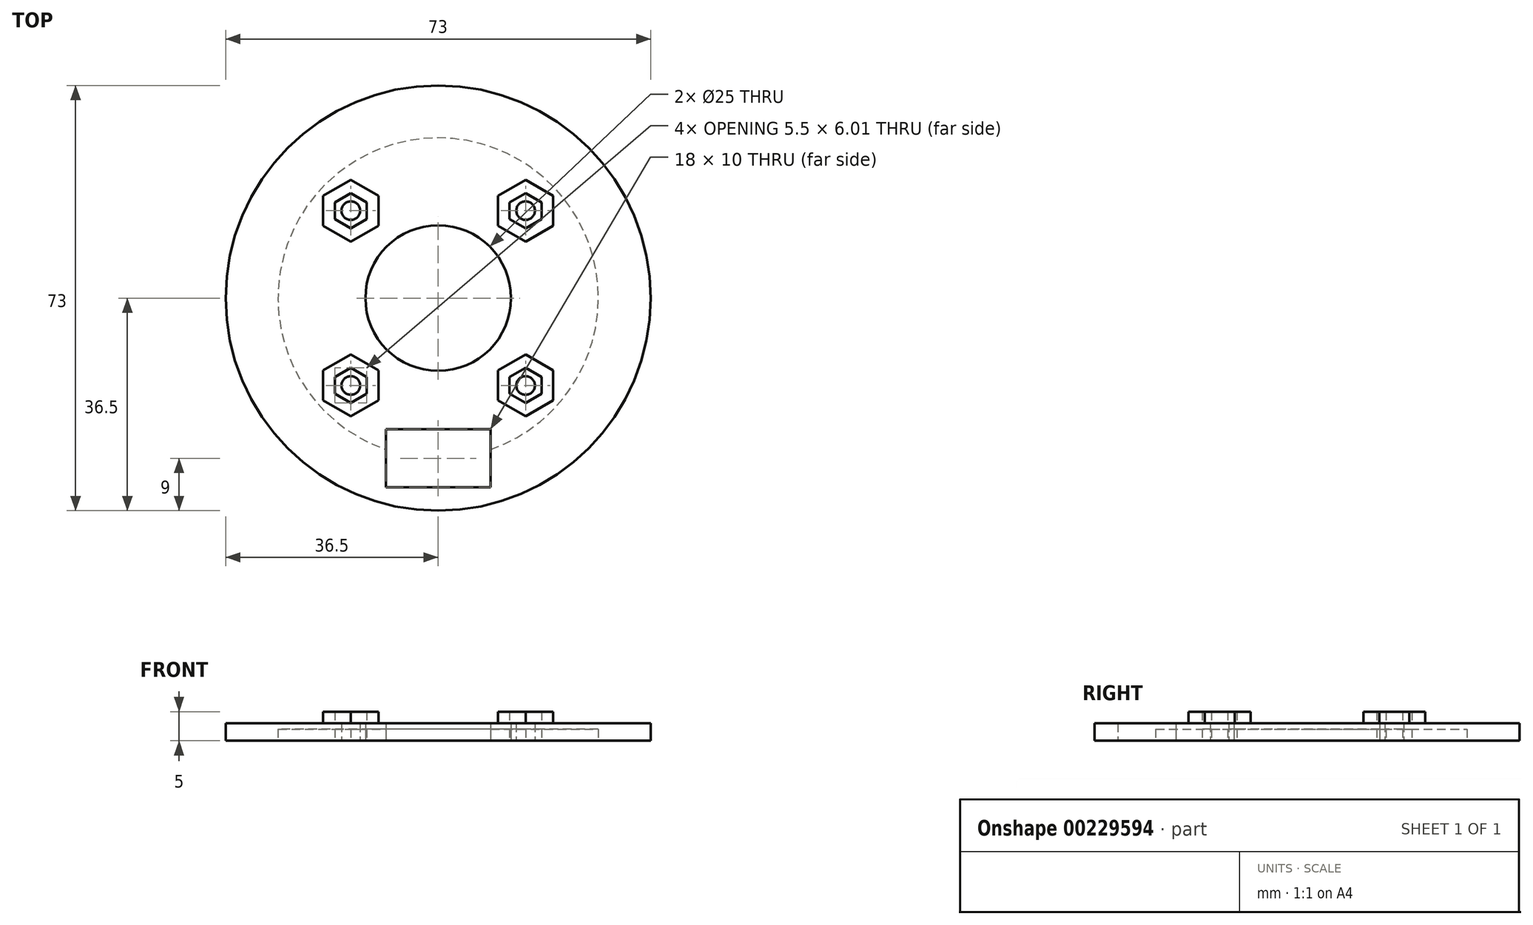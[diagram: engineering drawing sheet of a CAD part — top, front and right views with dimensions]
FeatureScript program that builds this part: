
annotation { "Feature Type Name" : "Feature", "Feature Type Description" : "" }
export const myFeature = defineFeature(function(context is Context, id is Id, definition is map)
    precondition{}
    {
        {
            var Q0;
            Q0=qCreatedBy(makeId("Top.planeOp"),FACE);
            var sketch = newSketch(context, id + "F0", { "sketchPlane" : qUnion([Q0])});
            skCircle(sketch, "E0", {"center": v(-15, 15) * mm, "radius": 1.6 * mm});
            skCircle(sketch, "E1", {"center": v(0, 0) * mm, "radius": 12.5 * mm});
            skLineSegment(sketch, "E2.bottom", {"start": v(9, -32.5) * mm, "end": v(-9, -32.5) * mm});
            skLineSegment(sketch, "E2.top", {"start": v(9, -22.5) * mm, "end": v(-9, -22.5) * mm});
            skLineSegment(sketch, "E2.left", {"start": v(9, -32.5) * mm, "end": v(9, -22.5) * mm});
            skLineSegment(sketch, "E2.right", {"start": v(-9, -32.5) * mm, "end": v(-9, -22.5) * mm});
            skPoint(sketch, "E2.middle", {"position": v(0, -27.5) * mm});
            skCircle(sketch, "E3", {"center": v(0, 0) * mm, "radius": 36.5 * mm});
            skLineSegment(sketch, "E4", {"start": v(-17.75, 16.42) * mm, "end": v(-17.75, 13.58) * mm});
            skLineSegment(sketch, "E5", {"start": v(-12.25, 16.42) * mm, "end": v(-12.25, 13.58) * mm});
            skLineSegment(sketch, "E6", {"start": v(-17.75, 16.42) * mm, "end": v(-15, 18) * mm});
            skLineSegment(sketch, "E7", {"start": v(-15, 18) * mm, "end": v(-12.25, 16.42) * mm});
            skLineSegment(sketch, "E8", {"start": v(-17.75, 13.58) * mm, "end": v(-15, 12) * mm});
            skLineSegment(sketch, "E9", {"start": v(-15, 12) * mm, "end": v(-12.25, 13.58) * mm});
            skLineSegment(sketch, "E10.0", {"start": v(-19.75, 12.43) * mm, "end": v(-15, 9.69) * mm});
            skLineSegment(sketch, "E10.1", {"start": v(-10.25, 17.57) * mm, "end": v(-10.25, 12.43) * mm});
            skLineSegment(sketch, "E10.2", {"start": v(-15, 20.31) * mm, "end": v(-10.25, 17.57) * mm});
            skLineSegment(sketch, "E10.3", {"start": v(-15, 9.69) * mm, "end": v(-10.25, 12.43) * mm});
            skLineSegment(sketch, "E10.4", {"start": v(-19.75, 17.57) * mm, "end": v(-15, 20.31) * mm});
            skLineSegment(sketch, "E10.5", {"start": v(-19.75, 17.57) * mm, "end": v(-19.75, 12.43) * mm});
            skLineSegment(sketch, "E11.MirrorCS", {"start": v(10.25, 17.57) * mm, "end": v(10.25, 12.43) * mm});
            skLineSegment(sketch, "E12.MirrorCS", {"start": v(12.25, 16.42) * mm, "end": v(12.25, 13.58) * mm});
            skLineSegment(sketch, "E13.MirrorCS", {"start": v(15, 18) * mm, "end": v(12.25, 16.42) * mm});
            skLineSegment(sketch, "E14.MirrorCS", {"start": v(19.75, 17.57) * mm, "end": v(19.75, 12.43) * mm});
            skLineSegment(sketch, "E15.MirrorCS", {"start": v(17.75, 16.42) * mm, "end": v(15, 18) * mm});
            skCircle(sketch, "E16.MirrorC", {"center": v(15, 15) * mm, "radius": 1.6 * mm});
            skLineSegment(sketch, "E17.MirrorCS", {"start": v(15, 9.69) * mm, "end": v(10.25, 12.43) * mm});
            skLineSegment(sketch, "E18.MirrorCS", {"start": v(19.75, 12.43) * mm, "end": v(15, 9.69) * mm});
            skLineSegment(sketch, "E19.MirrorCS", {"start": v(17.75, 16.42) * mm, "end": v(17.75, 13.58) * mm});
            skLineSegment(sketch, "E20.MirrorCS", {"start": v(19.75, 17.57) * mm, "end": v(15, 20.31) * mm});
            skLineSegment(sketch, "E21.MirrorCS", {"start": v(15, 20.31) * mm, "end": v(10.25, 17.57) * mm});
            skLineSegment(sketch, "E22.MirrorCS", {"start": v(15, 12) * mm, "end": v(12.25, 13.58) * mm});
            skLineSegment(sketch, "E23.MirrorCS", {"start": v(17.75, 13.58) * mm, "end": v(15, 12) * mm});
            skLineSegment(sketch, "E24.MirrorCS", {"start": v(-17.75, -13.58) * mm, "end": v(-15, -12) * mm});
            skLineSegment(sketch, "E25.MirrorCS", {"start": v(10.25, -17.57) * mm, "end": v(10.25, -12.43) * mm});
            skLineSegment(sketch, "E26.MirrorCS", {"start": v(-10.25, -17.57) * mm, "end": v(-10.25, -12.43) * mm});
            skLineSegment(sketch, "E27.MirrorCS", {"start": v(17.75, -13.58) * mm, "end": v(15, -12) * mm});
            skLineSegment(sketch, "E28.MirrorCS", {"start": v(15, -12) * mm, "end": v(12.25, -13.58) * mm});
            skLineSegment(sketch, "E29.MirrorCS", {"start": v(-15, -9.69) * mm, "end": v(-10.25, -12.43) * mm});
            skLineSegment(sketch, "E30.MirrorCS", {"start": v(15, -18) * mm, "end": v(12.25, -16.42) * mm});
            skLineSegment(sketch, "E31.MirrorCS", {"start": v(-12.25, -16.42) * mm, "end": v(-12.25, -13.58) * mm});
            skLineSegment(sketch, "E32.MirrorCS", {"start": v(-19.75, -12.43) * mm, "end": v(-15, -9.69) * mm});
            skLineSegment(sketch, "E33.MirrorCS", {"start": v(-15, -20.31) * mm, "end": v(-10.25, -17.57) * mm});
            skCircle(sketch, "E34.MirrorC", {"center": v(-15, -15) * mm, "radius": 1.6 * mm});
            skLineSegment(sketch, "E35.MirrorCS", {"start": v(-15, -18) * mm, "end": v(-12.25, -16.42) * mm});
            skLineSegment(sketch, "E36.MirrorCS", {"start": v(-19.75, -17.57) * mm, "end": v(-15, -20.31) * mm});
            skLineSegment(sketch, "E37.MirrorCS", {"start": v(15, -20.31) * mm, "end": v(10.25, -17.57) * mm});
            skLineSegment(sketch, "E38.MirrorCS", {"start": v(12.25, -16.42) * mm, "end": v(12.25, -13.58) * mm});
            skLineSegment(sketch, "E39.MirrorCS", {"start": v(-15, -12) * mm, "end": v(-12.25, -13.58) * mm});
            skLineSegment(sketch, "E40.MirrorCS", {"start": v(19.75, -17.57) * mm, "end": v(19.75, -12.43) * mm});
            skCircle(sketch, "E41.MirrorC", {"center": v(15, -15) * mm, "radius": 1.6 * mm});
            skLineSegment(sketch, "E42.MirrorCS", {"start": v(15, -9.69) * mm, "end": v(10.25, -12.43) * mm});
            skLineSegment(sketch, "E43.MirrorCS", {"start": v(-17.75, -16.42) * mm, "end": v(-17.75, -13.58) * mm});
            skLineSegment(sketch, "E44.MirrorCS", {"start": v(-17.75, -16.42) * mm, "end": v(-15, -18) * mm});
            skLineSegment(sketch, "E45.MirrorCS", {"start": v(17.75, -16.42) * mm, "end": v(15, -18) * mm});
            skLineSegment(sketch, "E46.MirrorCS", {"start": v(17.75, -16.42) * mm, "end": v(17.75, -13.58) * mm});
            skLineSegment(sketch, "E47.MirrorCS", {"start": v(19.75, -12.43) * mm, "end": v(15, -9.69) * mm});
            skLineSegment(sketch, "E48.MirrorCS", {"start": v(-19.75, -17.57) * mm, "end": v(-19.75, -12.43) * mm});
            skLineSegment(sketch, "E49.MirrorCS", {"start": v(19.75, -17.57) * mm, "end": v(15, -20.31) * mm});
            skCircle(sketch, "E50", {"center": v(0, 0) * mm, "radius": 27.5 * mm});
            skSolve(sketch);
        }
        {
            var Q0;
            Q0=makeQuery(id+"F0.imprint","IMPRINT",FACE,{"disambiguationData":[TD([[makeQuery(id+"F0.imprint","IMPRINT",EDGE,{"derivedFrom":sQuery(id+"F0.wireOp",EDGE,"E1")}),-1.0]])]});
            var Q1;
            Q1=makeQuery(id+"F0.imprint","IMPRINT",FACE,{"disambiguationData":[TD([[makeQuery(id+"F0.imprint","IMPRINT",EDGE,{"derivedFrom":sQuery(id+"F0.wireOp",EDGE,"E0")}),-1.0]])]});
            var Q2;
            Q2=makeQuery(id+"F0.imprint","IMPRINT",FACE,{"disambiguationData":[TD([[makeQuery(id+"F0.imprint","IMPRINT",EDGE,{"derivedFrom":sQuery(id+"F0.wireOp",EDGE,"29b6274b-2ecf-4a3f-908a-fa7b307661d00.MirrorC")}),1.0]])]});
            var Q3;
            Q3=makeQuery(id+"F0.imprint","IMPRINT",FACE,{"disambiguationData":[TD([[makeQuery(id+"F0.imprint","IMPRINT",EDGE,{"derivedFrom":sQuery(id+"F0.wireOp",EDGE,"d05b73d0-2f4d-47f0-b6ba-211effaf22bf0.MirrorC")}),-1.0]])]});
            var Q4;
            Q4=makeQuery(id+"F0.imprint","IMPRINT",FACE,{"disambiguationData":[TD([[makeQuery(id+"F0.imprint","IMPRINT",EDGE,{"derivedFrom":sQuery(id+"F0.wireOp",EDGE,"d05b73d0-2f4d-47f0-b6ba-211effaf22bf1.MirrorC")}),1.0]])]});
            var Q5;
            Q5=makeQuery(id+"F0.imprint","IMPRINT",FACE,{"disambiguationData":[TD([[makeQuery(id+"F0.imprint","IMPRINT",EDGE,{"derivedFrom":sQuery(id+"F0.wireOp",EDGE,"E4")}),-1.0]])]});
            var Q6;
            Q6=makeQuery(id+"F0.imprint","IMPRINT",FACE,{"disambiguationData":[TD([[makeQuery(id+"F0.imprint","IMPRINT",EDGE,{"derivedFrom":sQuery(id+"F0.wireOp",EDGE,"3b26f080-367b-4e38-8671-c6245af2c5290.MirrorCS")}),-1.0]])]});
            var Q7;
            Q7=makeQuery(id+"F0.imprint","IMPRINT",FACE,{"disambiguationData":[TD([[makeQuery(id+"F0.imprint","IMPRINT",EDGE,{"derivedFrom":sQuery(id+"F0.wireOp",EDGE,"2f9dc9b8-f9cd-4868-97b9-7f98089428e40.MirrorCS")}),-1.0]])]});
            var Q8;
            Q8=makeQuery(id+"F0.imprint","IMPRINT",FACE,{"disambiguationData":[TD([[makeQuery(id+"F0.imprint","IMPRINT",EDGE,{"derivedFrom":sQuery(id+"F0.wireOp",EDGE,"2f9dc9b8-f9cd-4868-97b9-7f98089428e46.MirrorCS")}),1.0]])]});
            var Q9;
            Q9=makeQuery(id+"F0.imprint","IMPRINT",FACE,{"disambiguationData":[TD([[makeQuery(id+"F0.imprint","IMPRINT",EDGE,{"derivedFrom":sQuery(id+"F0.wireOp",EDGE,"E24.MirrorCS")}),1.0]])]});
            var Q10;
            Q10=makeQuery(id+"F0.imprint","IMPRINT",FACE,{"disambiguationData":[TD([[makeQuery(id+"F0.imprint","IMPRINT",EDGE,{"derivedFrom":sQuery(id+"F0.wireOp",EDGE,"E24.MirrorCS")}),-1.0]])]});
            var Q11;
            Q11=makeQuery(id+"F0.imprint","IMPRINT",FACE,{"disambiguationData":[TD([[makeQuery(id+"F0.imprint","IMPRINT",EDGE,{"derivedFrom":sQuery(id+"F0.wireOp",EDGE,"E12.MirrorCS")}),-1.0]])]});
            var Q12;
            Q12=makeQuery(id+"F0.imprint","IMPRINT",FACE,{"disambiguationData":[TD([[makeQuery(id+"F0.imprint","IMPRINT",EDGE,{"derivedFrom":sQuery(id+"F0.wireOp",EDGE,"E12.MirrorCS")}),1.0]])]});
            var Q13;
            Q13=makeQuery(id+"F0.imprint","IMPRINT",FACE,{"disambiguationData":[TD([[makeQuery(id+"F0.imprint","IMPRINT",EDGE,{"derivedFrom":sQuery(id+"F0.wireOp",EDGE,"E27.MirrorCS")}),-1.0]])]});
            var Q14;
            Q14=makeQuery(id+"F0.imprint","IMPRINT",FACE,{"disambiguationData":[TD([[makeQuery(id+"F0.imprint","IMPRINT",EDGE,{"derivedFrom":sQuery(id+"F0.wireOp",EDGE,"E27.MirrorCS")}),1.0]])]});
            var Q15;
            {var subQ1=sQuery(id+"F0.wireOp",EDGE,"E2.bottom");Q15=makeQuery(id+"F0.imprint","IMPRINT",FACE,{"disambiguationData":[TD([[makeQuery(id+"F0.imprint","IMPRINT",EDGE,{"derivedFrom":subQ1}),1.0]])]});}
            extrude(context, id + "F1", {"entities" : qUnion([Q0, Q1, Q2, Q3, Q4, Q5, Q6, Q7, Q8, Q9, Q10, Q11, Q12, Q13, Q14, Q15]), "depth" : 3 * mm});
        }
        {
            var Q0;
            Q0=makeQuery(id+"F0.imprint","IMPRINT",FACE,{"disambiguationData":[TD([[makeQuery(id+"F0.imprint","IMPRINT",EDGE,{"derivedFrom":sQuery(id+"F0.wireOp",EDGE,"E4")}),-1.0]])]});
            var Q1;
            Q1=makeQuery(id+"F0.imprint","IMPRINT",FACE,{"disambiguationData":[TD([[makeQuery(id+"F0.imprint","IMPRINT",EDGE,{"derivedFrom":sQuery(id+"F0.wireOp",EDGE,"E24.MirrorCS")}),1.0]])]});
            var Q2;
            Q2=makeQuery(id+"F0.imprint","IMPRINT",FACE,{"disambiguationData":[TD([[makeQuery(id+"F0.imprint","IMPRINT",EDGE,{"derivedFrom":sQuery(id+"F0.wireOp",EDGE,"E12.MirrorCS")}),-1.0]])]});
            var Q3;
            Q3=makeQuery(id+"F0.imprint","IMPRINT",FACE,{"disambiguationData":[TD([[makeQuery(id+"F0.imprint","IMPRINT",EDGE,{"derivedFrom":sQuery(id+"F0.wireOp",EDGE,"E27.MirrorCS")}),-1.0]])]});
            extrude(context, id + "F2", {"entities" : qUnion([Q0, Q1, Q2, Q3]), "operationType" : NewBodyOperationType.ADD, "depth" : 5 * mm});
        }
        {
            var Q0;
            Q0=makeQuery(id+"F0.imprint","IMPRINT",FACE,{"disambiguationData":[TD([[makeQuery(id+"F0.imprint","IMPRINT",EDGE,{"derivedFrom":sQuery(id+"F0.wireOp",EDGE,"E1")}),-1.0]])]});
            var Q1;
            Q1=makeQuery(id+"F0.imprint","IMPRINT",FACE,{"disambiguationData":[TD([[makeQuery(id+"F0.imprint","IMPRINT",EDGE,{"derivedFrom":sQuery(id+"F0.wireOp",EDGE,"E4")}),-1.0]])]});
            var Q2;
            Q2=makeQuery(id+"F0.imprint","IMPRINT",FACE,{"disambiguationData":[TD([[makeQuery(id+"F0.imprint","IMPRINT",EDGE,{"derivedFrom":sQuery(id+"F0.wireOp",EDGE,"E12.MirrorCS")}),-1.0]])]});
            var Q3;
            Q3=makeQuery(id+"F0.imprint","IMPRINT",FACE,{"disambiguationData":[TD([[makeQuery(id+"F0.imprint","IMPRINT",EDGE,{"derivedFrom":sQuery(id+"F0.wireOp",EDGE,"E24.MirrorCS")}),1.0]])]});
            var Q4;
            Q4=makeQuery(id+"F0.imprint","IMPRINT",FACE,{"disambiguationData":[TD([[makeQuery(id+"F0.imprint","IMPRINT",EDGE,{"derivedFrom":sQuery(id+"F0.wireOp",EDGE,"E27.MirrorCS")}),-1.0]])]});
            extrude(context, id + "F3", {"entities" : qUnion([Q0, Q1, Q2, Q3, Q4]), "depth" : 2 * mm});
        }
    });
